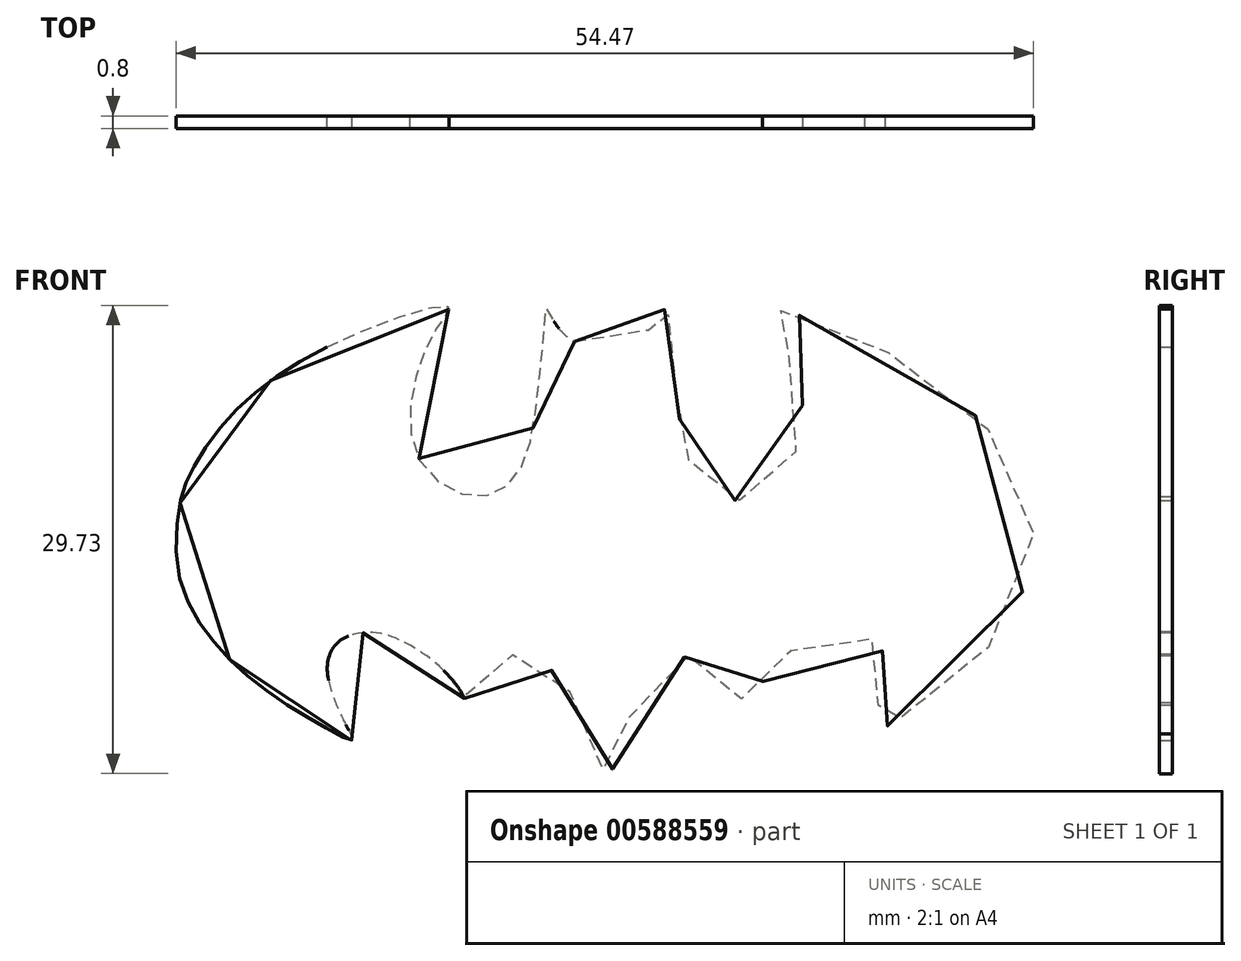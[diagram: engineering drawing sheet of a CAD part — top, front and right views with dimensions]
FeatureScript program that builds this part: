
annotation { "Feature Type Name" : "Feature", "Feature Type Description" : "" }
export const myFeature = defineFeature(function(context is Context, id is Id, definition is map)
    precondition{}
    {
        {
            var Q0;
            Q0=qCreatedBy(makeId("Front.planeOp"),FACE);
            var sketch = newSketch(context, id + "F0", { "sketchPlane" : qUnion([Q0])});
            skPoint(sketch, "E0.36.internal.snap0", {"position": v(0, 28.5) * mm});
            skPoint(sketch, "E0.55.internal.snap0", {"position": v(0, 28.5) * mm});
            skPoint(sketch, "E0.57.internal.snap0", {"position": v(0, 28.5) * mm});
            skFitSpline(sketch, "E0", {"points": [v(-30.63, 47.46) * mm, v(-26.45, 47.42) * mm, v(-26.42, 47.46) * mm, v(-26.03, 48.07) * mm, v(-25.57, 48.53) * mm, v(-25.25, 49.05) * mm, v(-24.86, 49.5) * mm, v(-24.73, 49.6) * mm, v(-24.68, 49.29) * mm, v(-24.54, 47.8) * mm, v(-24.33, 45.65) * mm, v(-23.93, 42.23) * mm, v(-23.75, 41.1) * mm, v(-23.39, 39.91) * mm, v(-22.16, 38.28) * mm, v(-20.78, 37.4) * mm, v(-19.35, 37.55) * mm, v(-17.52, 38.73) * mm, v(-16.29, 41.32) * mm, v(-16.23, 43.87) * mm, v(-17.9, 48.18) * mm, v(-18.66, 49.43) * mm, v(-17.6, 49.43) * mm, v(-13.66, 48.13) * mm, v(-8.04, 45.19) * mm, v(-3.94, 41.35) * mm, v(-1.66, 36.94) * mm, v(-2.1, 31.67) * mm, v(-5.32, 26.94) * mm, v(-8.85, 24.22) * mm, v(-12.01, 22.52) * mm, v(-12.15, 22.84) * mm, v(-11.34, 24.26) * mm, v(-10.9, 26.36) * mm, v(-11.17, 27.97) * mm, v(-12.82, 29) * mm, v(-15.72, 28.5) * mm, v(-18.26, 26.36) * mm, v(-19.82, 24.35) * mm, v(-20.09, 24.93) * mm, v(-21.52, 26.9) * mm, v(-22.95, 27.52) * mm, v(-25.18, 26.5) * mm, v(-26.92, 23.95) * mm, v(-27.8, 22.12) * mm, v(-28.39, 20.03) * mm, v(-28.88, 20.38) * mm, v(-29.55, 23.1) * mm, v(-31.07, 25.38) * mm, v(-32.72, 27.16) * mm, v(-34, 27.61) * mm, v(-36.06, 26.58) * mm, v(-37.31, 24.53) * mm, v(-37.9, 25.3) * mm, v(-39.9, 27.39) * mm, v(-41.77, 28.5) * mm, v(-43.25, 28.95) * mm, v(-45.43, 28.5) * mm, v(-46.32, 26.54) * mm, v(-45.16, 23.15) * mm, v(-44.76, 22.12) * mm, v(-45.83, 22.57) * mm, v(-48.55, 24.18) * mm, v(-51.68, 26.45) * mm, v(-54.18, 29.22) * mm, v(-55.78, 32.79) * mm, v(-55.65, 37.3) * mm, v(-54.9, 39.3) * mm, v(-52.97, 42.16) * mm, v(-49.85, 45.01) * mm, v(-44.36, 48) * mm, v(-38.7, 49.7) * mm, v(-38.65, 49.38) * mm, v(-39.45, 48.18) * mm, v(-40.88, 44.39) * mm, v(-40.39, 39.8) * mm, v(-36.9, 37.6) * mm, v(-34.28, 38.99) * mm, v(-33.03, 43.58) * mm, v(-32.5, 49.03) * mm, v(-32.4, 49.56) * mm, v(-30.63, 47.46) * mm]});
            skSolve(sketch);
        }
        {
            var Q0;
            Q0=makeQuery(id+"F0.imprint","IMPRINT",FACE,{"disambiguationData":[TD([[makeQuery(id+"F0.imprint","IMPRINT",EDGE,{"derivedFrom":sQuery(id+"F0.wireOp",EDGE,"E0")}),-1.0]])]});
            extrude(context, id + "F1", {"entities" : qUnion([Q0]), "depth" : 0.8 * mm, "offsetDistance" : 25 * mm});
        }
    });
